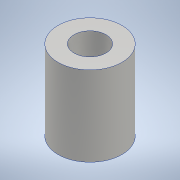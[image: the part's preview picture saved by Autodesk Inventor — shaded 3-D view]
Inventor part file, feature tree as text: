
AUTODESK INVENTOR PART (.ipt)
format: ipt  version: 2020.2 (Build 242310000, 310)  size: 100,352 bytes
history: native  units: mm
features: other x1, extrude x1, sketch x1
ambient origin geometry x8: Origin, YZ Plane, XZ Plane, XY Plane, X Axis, Y Axis, Z Axis, Center Point
bodies: Body1 (feature_tree)
feature tree (3):
  other  "ソリッド1"
  extrude  "押し出し1"  Depth=4.0mm
  sketch  "スケッチ1"
